# Revit family: Sink-Lavatory-KOHLER-Rhythm-K-2602
name_source: partatom
category: Plumbing Fixtures
revit_build: Autodesk Revit 2015 (Build: 20140606_1530(x64)
units: mm (PartAtom-declared; Revit-internal decimal feet)

## types (4) — shared parameters
ADA Compliant = Yes
Assembly Code = D2010400
CW Connection = No
Cold Water Inlet = Cold Water Inlet
Date Modified = 01/17/2019
Default Elevation = 34"
Drain Included = No
HW Connection = No
Height = 6 1/4"
Hot Water Inlet = Hot Water Inlet
Length = 23 1/8"
Manufacturer = KOHLER Co.
MasterFormat 1995 = 15410
MasterFormat 2004 = 22.41.16
Material = 20 Gauge Stainless Steel
Product Documentation Link = https://www.us.kohler.com
Product Name = Rhythm
Product Page URL = http://www.us.kohler.com
URL = https://www.us.kohler.com
Vent Connection = No
Waste Connection = Yes
Waste Water Outlet = Waste Water Outlet
Width = 15 1/4"

## per-type parameters (varying)
| type | Description | Finish | Model | Type |
| SU-Satin Finish | Elliptical under-mount bathroom sink with satin finish | Kohler-Metal-SU-Stainless_Steel_Luster_Finish | K-2602-SU-NA | 1 |
| MU-Mirror Finish | Oval under-mount bathroom sink with Mirror finish | Kohler-Metal-MU-Stainless_Steel_Mirror_Finish | K-2602-MU-NA | 2 |
| MF-Mirror French Gold | Oval under-mount bathroom sink | Kohler-Metal-MF-Mirrored_French_Gold | K-2602-MF | 3 |
| SBV-Satin Bronze | Oval under-mount bathroom sink | Kohler-Metal-SBV-Satin_Bronze | K-2602-SBV | 4 |

## geometry (parser evidence)
native form markers: Sweep x6
no freeform markers — native parametric forms only
